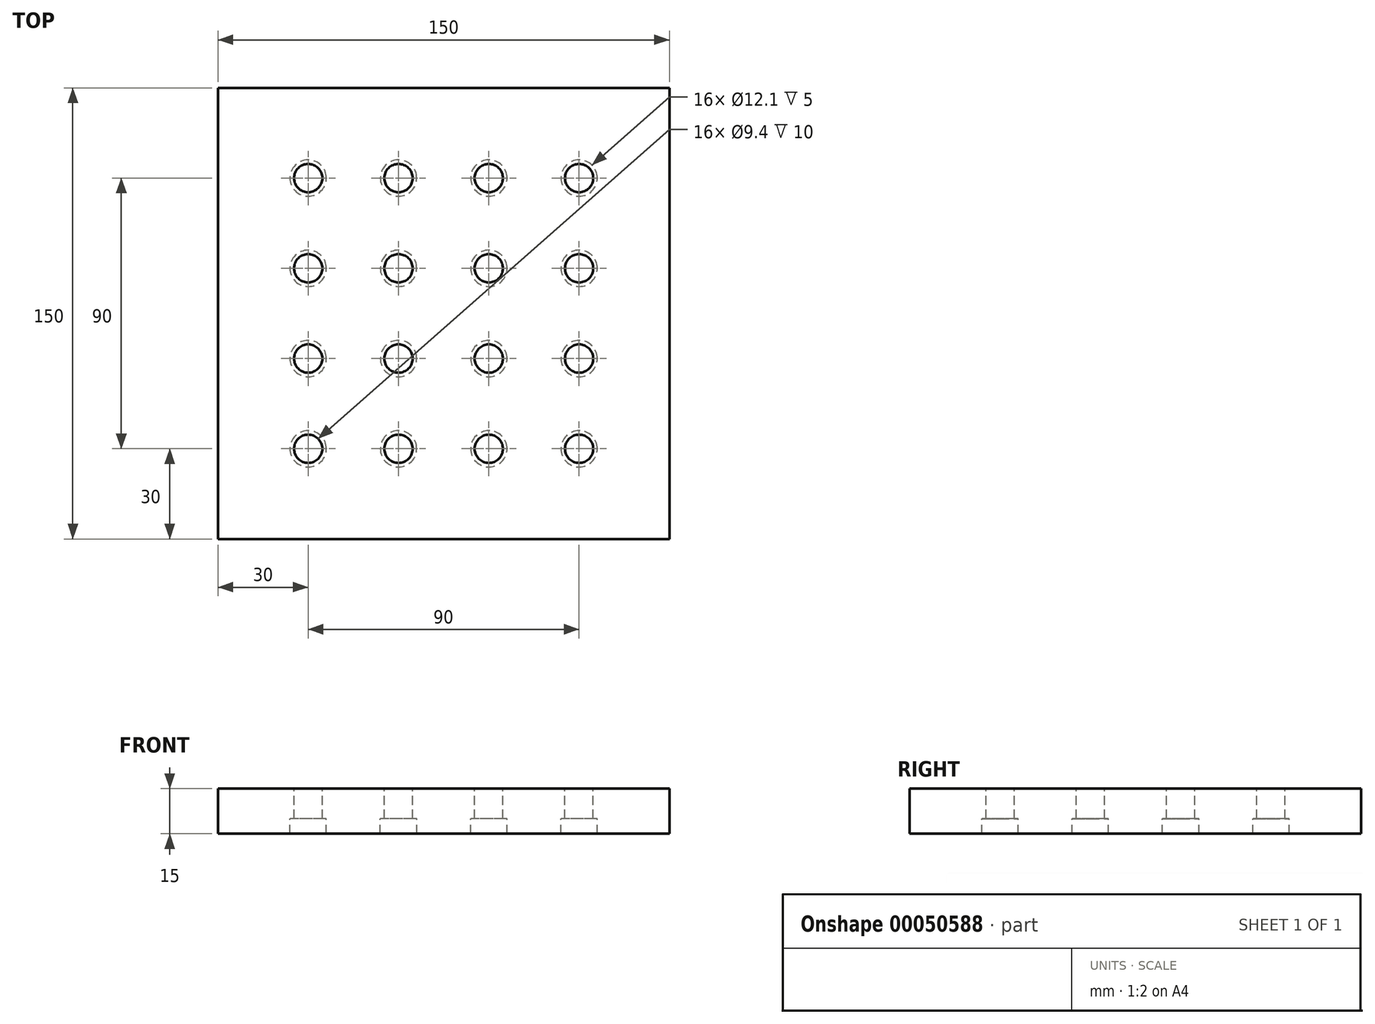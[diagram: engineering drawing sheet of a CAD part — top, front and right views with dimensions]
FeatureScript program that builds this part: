
annotation { "Feature Type Name" : "Feature", "Feature Type Description" : "" }
export const myFeature = defineFeature(function(context is Context, id is Id, definition is map)
    precondition{}
    {
        {
            var Q0;
            Q0=qCreatedBy(makeId("Top.planeOp"),FACE);
            var sketch = newSketch(context, id + "F0", { "sketchPlane" : qUnion([Q0])});
            skLineSegment(sketch, "E0.bottom", {"start": v(0, 0) * mm, "end": v(-150, 0) * mm});
            skLineSegment(sketch, "E0.top", {"start": v(0, 150) * mm, "end": v(-150, 150) * mm});
            skLineSegment(sketch, "E0.left", {"start": v(0, 0) * mm, "end": v(0, 150) * mm});
            skLineSegment(sketch, "E0.right", {"start": v(-150, 0) * mm, "end": v(-150, 150) * mm});
            skCircle(sketch, "E1", {"center": v(-120, 30) * mm, "radius": 6.05 * mm});
            skCircle(sketch, "E2", {"center": v(-120, 30) * mm, "radius": 4.7 * mm});
            skCircle(sketch, "E3.0.1.0", {"center": v(-120, 60) * mm, "radius": 6.05 * mm});
            skCircle(sketch, "E3.0.1.1", {"center": v(-120, 60) * mm, "radius": 4.7 * mm});
            skCircle(sketch, "E3.0.2.0", {"center": v(-120, 90) * mm, "radius": 6.05 * mm});
            skCircle(sketch, "E3.0.2.1", {"center": v(-120, 90) * mm, "radius": 4.7 * mm});
            skCircle(sketch, "E3.0.3.0", {"center": v(-120, 120) * mm, "radius": 6.05 * mm});
            skCircle(sketch, "E3.0.3.1", {"center": v(-120, 120) * mm, "radius": 4.7 * mm});
            skCircle(sketch, "E3.1.0.0", {"center": v(-90, 30) * mm, "radius": 6.05 * mm});
            skCircle(sketch, "E3.1.0.1", {"center": v(-90, 30) * mm, "radius": 4.7 * mm});
            skCircle(sketch, "E3.1.1.0", {"center": v(-90, 60) * mm, "radius": 6.05 * mm});
            skCircle(sketch, "E3.1.1.1", {"center": v(-90, 60) * mm, "radius": 4.7 * mm});
            skCircle(sketch, "E3.1.2.0", {"center": v(-90, 90) * mm, "radius": 6.05 * mm});
            skCircle(sketch, "E3.1.2.1", {"center": v(-90, 90) * mm, "radius": 4.7 * mm});
            skCircle(sketch, "E3.1.3.0", {"center": v(-90, 120) * mm, "radius": 6.05 * mm});
            skCircle(sketch, "E3.1.3.1", {"center": v(-90, 120) * mm, "radius": 4.7 * mm});
            skCircle(sketch, "E3.2.0.0", {"center": v(-60, 30) * mm, "radius": 6.05 * mm});
            skCircle(sketch, "E3.2.0.1", {"center": v(-60, 30) * mm, "radius": 4.7 * mm});
            skCircle(sketch, "E3.2.1.0", {"center": v(-60, 60) * mm, "radius": 6.05 * mm});
            skCircle(sketch, "E3.2.1.1", {"center": v(-60, 60) * mm, "radius": 4.7 * mm});
            skCircle(sketch, "E3.2.2.0", {"center": v(-60, 90) * mm, "radius": 6.05 * mm});
            skCircle(sketch, "E3.2.2.1", {"center": v(-60, 90) * mm, "radius": 4.7 * mm});
            skCircle(sketch, "E3.2.3.0", {"center": v(-60, 120) * mm, "radius": 6.05 * mm});
            skCircle(sketch, "E3.2.3.1", {"center": v(-60, 120) * mm, "radius": 4.7 * mm});
            skCircle(sketch, "E3.3.0.0", {"center": v(-30, 30) * mm, "radius": 6.05 * mm});
            skCircle(sketch, "E3.3.0.1", {"center": v(-30, 30) * mm, "radius": 4.7 * mm});
            skCircle(sketch, "E3.3.1.0", {"center": v(-30, 60) * mm, "radius": 6.05 * mm});
            skCircle(sketch, "E3.3.1.1", {"center": v(-30, 60) * mm, "radius": 4.7 * mm});
            skCircle(sketch, "E3.3.2.0", {"center": v(-30, 90) * mm, "radius": 6.05 * mm});
            skCircle(sketch, "E3.3.2.1", {"center": v(-30, 90) * mm, "radius": 4.7 * mm});
            skCircle(sketch, "E3.3.3.0", {"center": v(-30, 120) * mm, "radius": 6.05 * mm});
            skCircle(sketch, "E3.3.3.1", {"center": v(-30, 120) * mm, "radius": 4.7 * mm});
            skLineSegment(sketch, "E3.direction1", {"start": v(-120, 30) * mm, "end": v(-90, 30) * mm, "construction": true});
            skLineSegment(sketch, "E3.direction2", {"start": v(-120, 30) * mm, "end": v(-120, 60) * mm, "construction": true});
            skSolve(sketch);
        }
        {
            var Q0;
            Q0=makeQuery(id+"F0.imprint","IMPRINT",FACE,{"disambiguationData":[TD([[makeQuery(id+"F0.imprint","IMPRINT",EDGE,{"derivedFrom":sQuery(id+"F0.wireOp",EDGE,"E0.bottom")}),-1.0]])]});
            var Q1;
            Q1=makeQuery(id+"F0.imprint","IMPRINT",FACE,{"disambiguationData":[TD([[makeQuery(id+"F0.imprint","IMPRINT",EDGE,{"derivedFrom":sQuery(id+"F0.wireOp",EDGE,"E1")}),1.0]])]});
            var Q2;
            Q2=makeQuery(id+"F0.imprint","IMPRINT",FACE,{"disambiguationData":[TD([[makeQuery(id+"F0.imprint","IMPRINT",EDGE,{"derivedFrom":sQuery(id+"F0.wireOp",EDGE,"E2")}),1.0]])]});
            extrude(context, id + "F1", {"entities" : qUnion([Q0, Q1, Q2]), "oppositeDirection" : true, "depth" : 15 * mm});
        }
        {
            var Q0;
            Q0=makeQuery(id+"F0.imprint","IMPRINT",FACE,{"disambiguationData":[TD([[makeQuery(id+"F0.imprint","IMPRINT",EDGE,{"derivedFrom":sQuery(id+"F0.wireOp",EDGE,"E2")}),1.0]])]});
            extrude(context, id + "F2", {"entities" : qUnion([Q0]), "operationType" : NewBodyOperationType.REMOVE, "oppositeDirection" : true, "depth" : 15 * mm});
        }
        {
            var Q0;
            Q0=makeQuery(id+"F0.imprint","IMPRINT",FACE,{"disambiguationData":[TD([[makeQuery(id+"F0.imprint","IMPRINT",EDGE,{"derivedFrom":sQuery(id+"F0.wireOp",EDGE,"E1")}),1.0]])]});
            extrude(context, id + "F3", {"entities" : qUnion([Q0]), "operationType" : NewBodyOperationType.REMOVE, "oppositeDirection" : true, "depth" : 10 * mm});
        }
        {
            var Q0;
            Q0=makeQuery(id+"F0.imprint","IMPRINT",FACE,{"disambiguationData":[TD([[makeQuery(id+"F0.imprint","IMPRINT",EDGE,{"derivedFrom":sQuery(id+"F0.wireOp",EDGE,"E3.0.1.0")}),1.0]])]});
            var Q1;
            Q1=makeQuery(id+"F0.imprint","IMPRINT",FACE,{"disambiguationData":[TD([[makeQuery(id+"F0.imprint","IMPRINT",EDGE,{"derivedFrom":sQuery(id+"F0.wireOp",EDGE,"E3.0.2.0")}),1.0]])]});
            var Q2;
            Q2=makeQuery(id+"F0.imprint","IMPRINT",FACE,{"disambiguationData":[TD([[makeQuery(id+"F0.imprint","IMPRINT",EDGE,{"derivedFrom":sQuery(id+"F0.wireOp",EDGE,"E3.0.3.0")}),1.0]])]});
            var Q3;
            Q3=makeQuery(id+"F0.imprint","IMPRINT",FACE,{"disambiguationData":[TD([[makeQuery(id+"F0.imprint","IMPRINT",EDGE,{"derivedFrom":sQuery(id+"F0.wireOp",EDGE,"E3.1.3.0")}),1.0]])]});
            var Q4;
            Q4=makeQuery(id+"F0.imprint","IMPRINT",FACE,{"disambiguationData":[TD([[makeQuery(id+"F0.imprint","IMPRINT",EDGE,{"derivedFrom":sQuery(id+"F0.wireOp",EDGE,"E3.2.3.0")}),1.0]])]});
            var Q5;
            Q5=makeQuery(id+"F0.imprint","IMPRINT",FACE,{"disambiguationData":[TD([[makeQuery(id+"F0.imprint","IMPRINT",EDGE,{"derivedFrom":sQuery(id+"F0.wireOp",EDGE,"E3.1.2.0")}),1.0]])]});
            var Q6;
            Q6=makeQuery(id+"F0.imprint","IMPRINT",FACE,{"disambiguationData":[TD([[makeQuery(id+"F0.imprint","IMPRINT",EDGE,{"derivedFrom":sQuery(id+"F0.wireOp",EDGE,"E3.1.1.0")}),1.0]])]});
            var Q7;
            Q7=makeQuery(id+"F0.imprint","IMPRINT",FACE,{"disambiguationData":[TD([[makeQuery(id+"F0.imprint","IMPRINT",EDGE,{"derivedFrom":sQuery(id+"F0.wireOp",EDGE,"E3.2.2.0")}),1.0]])]});
            var Q8;
            Q8=makeQuery(id+"F0.imprint","IMPRINT",FACE,{"disambiguationData":[TD([[makeQuery(id+"F0.imprint","IMPRINT",EDGE,{"derivedFrom":sQuery(id+"F0.wireOp",EDGE,"E3.3.2.0")}),1.0]])]});
            var Q9;
            Q9=makeQuery(id+"F0.imprint","IMPRINT",FACE,{"disambiguationData":[TD([[makeQuery(id+"F0.imprint","IMPRINT",EDGE,{"derivedFrom":sQuery(id+"F0.wireOp",EDGE,"E3.3.1.0")}),1.0]])]});
            var Q10;
            Q10=makeQuery(id+"F0.imprint","IMPRINT",FACE,{"disambiguationData":[TD([[makeQuery(id+"F0.imprint","IMPRINT",EDGE,{"derivedFrom":sQuery(id+"F0.wireOp",EDGE,"E3.2.1.0")}),1.0]])]});
            var Q11;
            Q11=makeQuery(id+"F0.imprint","IMPRINT",FACE,{"disambiguationData":[TD([[makeQuery(id+"F0.imprint","IMPRINT",EDGE,{"derivedFrom":sQuery(id+"F0.wireOp",EDGE,"E3.2.0.0")}),1.0]])]});
            var Q12;
            Q12=makeQuery(id+"F0.imprint","IMPRINT",FACE,{"disambiguationData":[TD([[makeQuery(id+"F0.imprint","IMPRINT",EDGE,{"derivedFrom":sQuery(id+"F0.wireOp",EDGE,"E3.1.0.0")}),1.0]])]});
            var Q13;
            Q13=makeQuery(id+"F0.imprint","IMPRINT",FACE,{"disambiguationData":[TD([[makeQuery(id+"F0.imprint","IMPRINT",EDGE,{"derivedFrom":sQuery(id+"F0.wireOp",EDGE,"E3.3.3.0")}),1.0]])]});
            var Q14;
            Q14=makeQuery(id+"F0.imprint","IMPRINT",FACE,{"disambiguationData":[TD([[makeQuery(id+"F0.imprint","IMPRINT",EDGE,{"derivedFrom":sQuery(id+"F0.wireOp",EDGE,"E3.3.0.0")}),1.0]])]});
            var Q15;
            Q15=makeQuery(id+"F0.imprint","IMPRINT",FACE,{"disambiguationData":[TD([[makeQuery(id+"F0.imprint","IMPRINT",EDGE,{"derivedFrom":sQuery(id+"F0.wireOp",EDGE,"E1")}),1.0]])]});
            extrude(context, id + "F4", {"entities" : qUnion([Q0, Q1, Q2, Q3, Q4, Q5, Q6, Q7, Q8, Q9, Q10, Q11, Q12, Q13, Q14, Q15]), "operationType" : NewBodyOperationType.ADD, "oppositeDirection" : true, "depth" : 10 * mm});
        }
        {
            var Q0;
            Q0=makeQuery(id+"F0.imprint","IMPRINT",FACE,{"disambiguationData":[TD([[makeQuery(id+"F0.imprint","IMPRINT",EDGE,{"derivedFrom":sQuery(id+"F0.wireOp",EDGE,"E1")}),1.0]])]});
            extrude(context, id + "F5", {"entities" : qUnion([Q0]), "operationType" : NewBodyOperationType.REMOVE, "oppositeDirection" : true, "depth" : 10 * mm});
        }
        {
            var Q0;
            Q0=makeQuery(id+"F0.imprint","IMPRINT",FACE,{"disambiguationData":[TD([[makeQuery(id+"F0.imprint","IMPRINT",EDGE,{"derivedFrom":sQuery(id+"F0.wireOp",EDGE,"E1")}),1.0]])]});
            extrude(context, id + "F6", {"entities" : qUnion([Q0]), "operationType" : NewBodyOperationType.REMOVE, "oppositeDirection" : true, "depth" : 25 * mm});
        }
        {
            var Q0;
            Q0=makeQuery(id+"F0.imprint","IMPRINT",FACE,{"disambiguationData":[TD([[makeQuery(id+"F0.imprint","IMPRINT",EDGE,{"derivedFrom":sQuery(id+"F0.wireOp",EDGE,"E1")}),1.0]])]});
            extrude(context, id + "F7", {"entities" : qUnion([Q0]), "operationType" : NewBodyOperationType.ADD, "oppositeDirection" : true, "depth" : 10 * mm});
        }
    });
